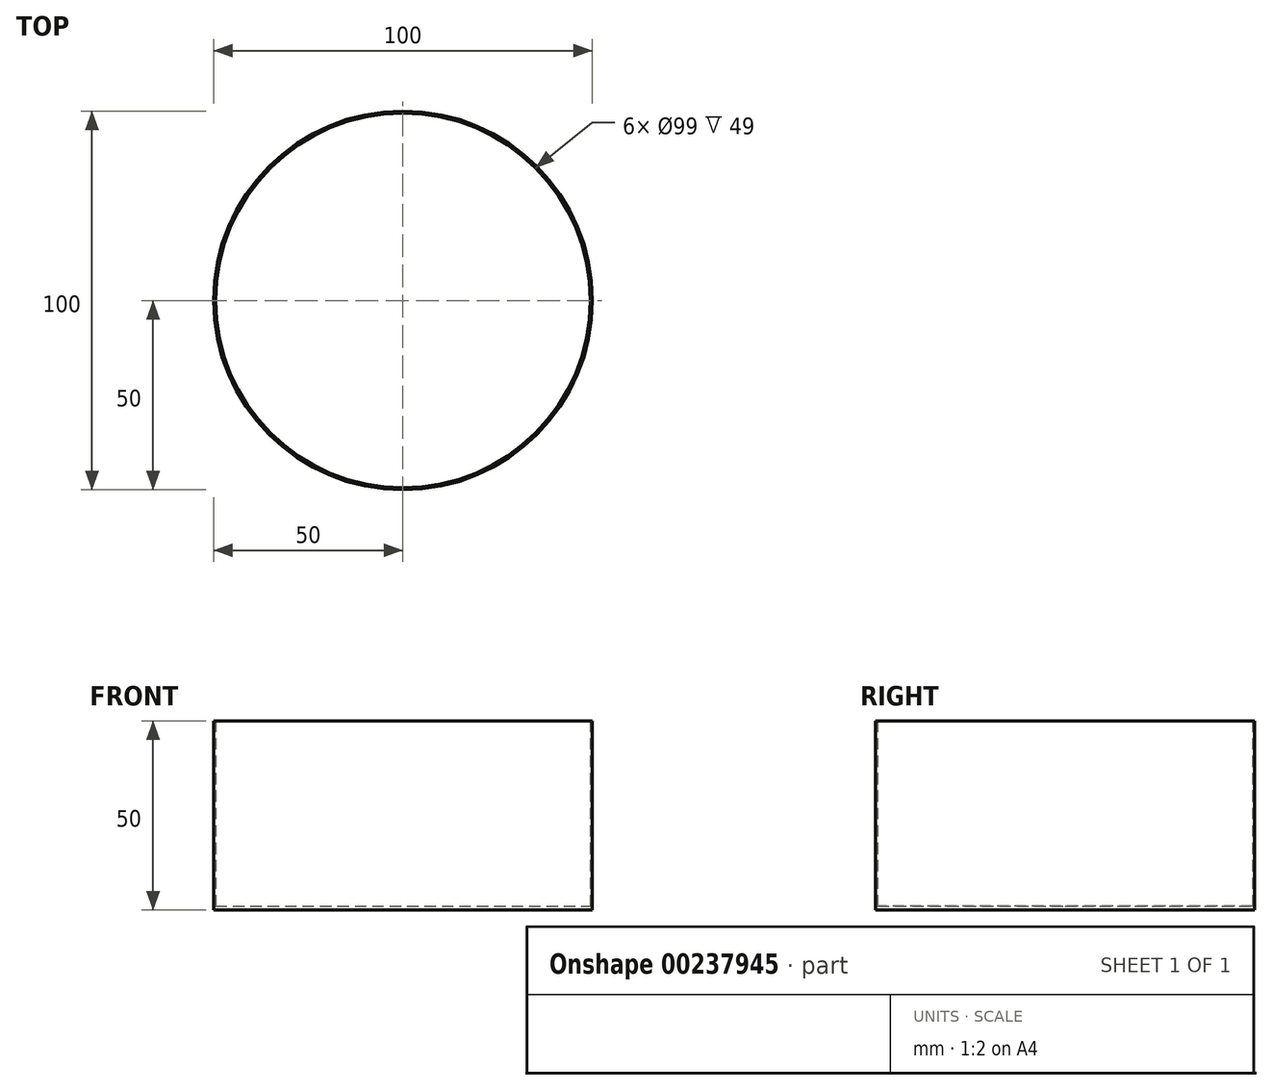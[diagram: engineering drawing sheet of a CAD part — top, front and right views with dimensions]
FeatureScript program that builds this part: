
annotation { "Feature Type Name" : "Feature", "Feature Type Description" : "" }
export const myFeature = defineFeature(function(context is Context, id is Id, definition is map)
    precondition{}
    {
        {
            var Q0;
            Q0=qCreatedBy(makeId("Front.planeOp"),FACE);
            var sketch = newSketch(context, id + "F0", { "sketchPlane" : qUnion([Q0])});
            skLineSegment(sketch, "E0", {"start": v(-50, 49) * mm, "end": v(-49.5, 49) * mm});
            skLineSegment(sketch, "E1", {"start": v(-50, 49) * mm, "end": v(-50, 0) * mm});
            skLineSegment(sketch, "E2", {"start": v(-49.5, 49) * mm, "end": v(-49.5, 0) * mm});
            skLineSegment(sketch, "E3", {"start": v(-50, 0) * mm, "end": v(-50, -1) * mm});
            skLineSegment(sketch, "E4", {"start": v(-50, -1) * mm, "end": v(0, -1) * mm});
            skLineSegment(sketch, "E5", {"start": v(-49.5, 0) * mm, "end": v(0, 0) * mm});
            skLineSegment(sketch, "E6", {"start": v(0, -1) * mm, "end": v(0, 0) * mm});
            skSolve(sketch);
        }
        {
            var Q0;
            Q0 = qSketchRegion(id + "F0", true);
            var Q1;
            Q1=sQuery(id+"F0.wireOp",EDGE,"E6");
            revolve(context, id + "F1", {"entities" : qUnion([Q0]), "axis" : qUnion([Q1]), "revolveType" : RevolveType.FULL});
        }
    });
